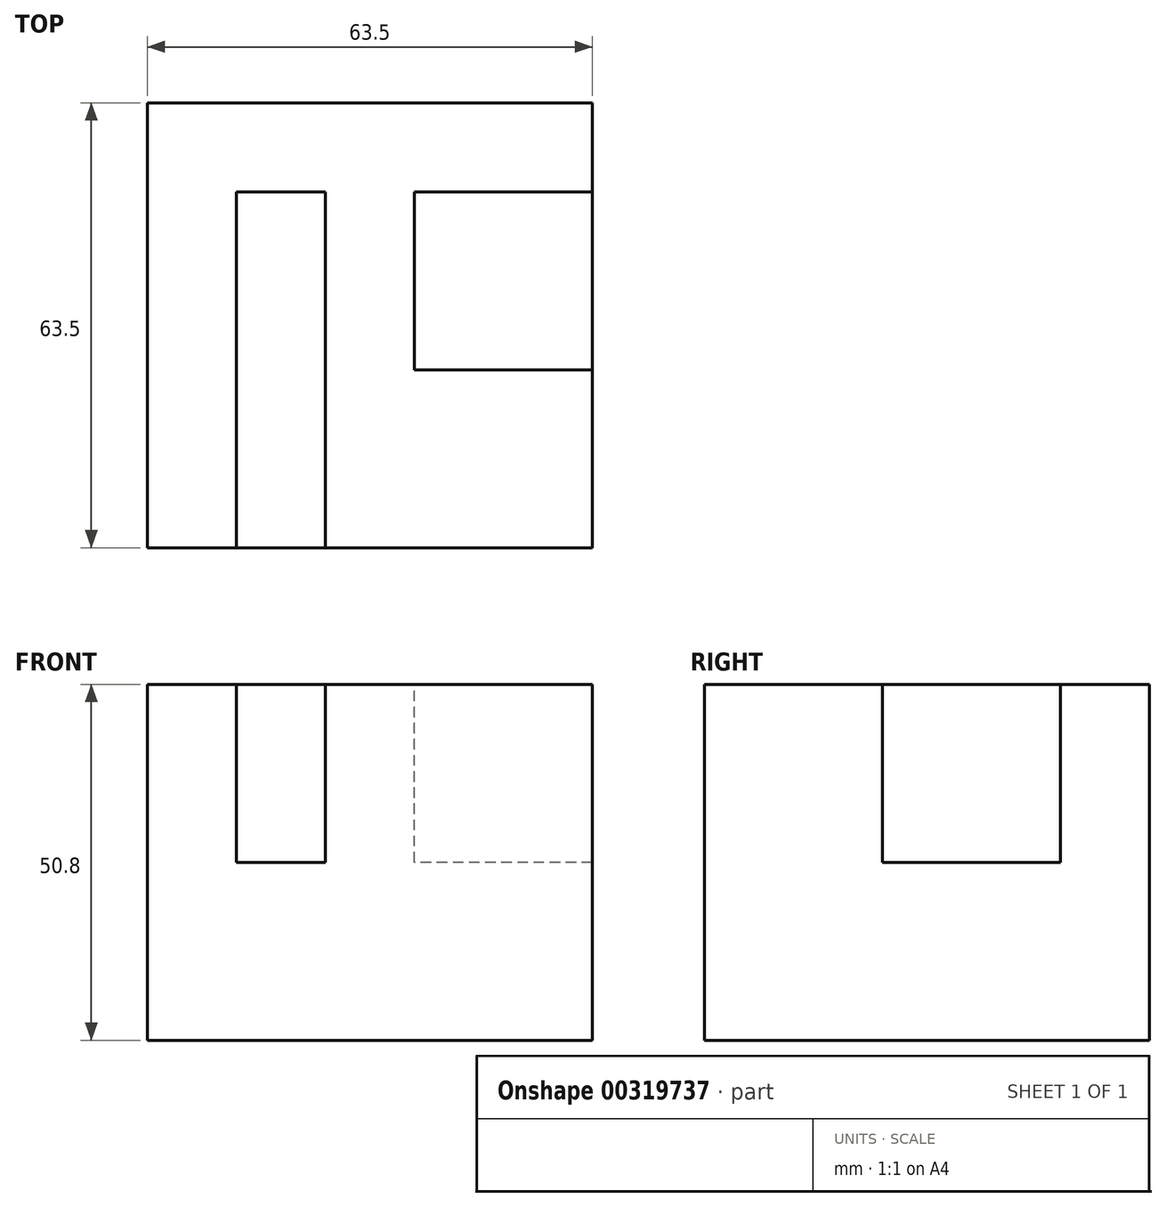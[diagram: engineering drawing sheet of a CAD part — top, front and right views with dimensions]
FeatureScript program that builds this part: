
annotation { "Feature Type Name" : "Feature", "Feature Type Description" : "" }
export const myFeature = defineFeature(function(context is Context, id is Id, definition is map)
    precondition{}
    {
        {
            var Q0;
            Q0=qCreatedBy(makeId("Top.planeOp"),FACE);
            var sketch = newSketch(context, id + "F0", { "sketchPlane" : qUnion([Q0])});
            skLineSegment(sketch, "E0", {"start": v(-27.52, -48.66) * mm, "end": v(35.98, -48.66) * mm});
            skLineSegment(sketch, "E1", {"start": v(35.98, -48.66) * mm, "end": v(35.98, 14.84) * mm});
            skLineSegment(sketch, "E2", {"start": v(35.98, 14.84) * mm, "end": v(-27.52, 14.84) * mm});
            skLineSegment(sketch, "E3", {"start": v(-27.52, 14.84) * mm, "end": v(-27.52, -48.66) * mm});
            skSolve(sketch);
        }
        {
            var Q0;
            Q0=makeQuery(id+"F0.imprint","IMPRINT",FACE,{"disambiguationData":[TD([[makeQuery(id+"F0.imprint","IMPRINT",EDGE,{"derivedFrom":sQuery(id+"F0.wireOp",EDGE,"E0")}),1.0]])]});
            extrude(context, id + "F1", {"entities" : qUnion([Q0]), "depth" : 50.8 * mm});
        }
        {
            var Q0;
            Q0=makeQuery(id+"F1.opExtrude","CAP_FACE",FACE,{"disambiguationData":[OSD([sQuery(id+"F0.wireOp",EDGE,"E0"),sQuery(id+"F0.wireOp",EDGE,"E1"),sQuery(id+"F0.wireOp",EDGE,"E2"),sQuery(id+"F0.wireOp",EDGE,"E3")])],"isStart":false});
            var sketch = newSketch(context, id + "F2", { "sketchPlane" : qUnion([Q0])});
            skLineSegment(sketch, "E4", {"start": v(-14.82, -48.66) * mm, "end": v(-14.82, 2.14) * mm});
            skLineSegment(sketch, "E5", {"start": v(-14.82, 2.14) * mm, "end": v(-2.12, 2.14) * mm});
            skLineSegment(sketch, "E6", {"start": v(-2.12, 2.14) * mm, "end": v(-2.12, -48.66) * mm});
            skLineSegment(sketch, "E7", {"start": v(35.98, 2.14) * mm, "end": v(10.58, 2.14) * mm});
            skLineSegment(sketch, "E8", {"start": v(10.58, 2.14) * mm, "end": v(10.58, -23.26) * mm});
            skLineSegment(sketch, "E9", {"start": v(10.58, -23.26) * mm, "end": v(35.98, -23.26) * mm});
            skLineSegment(sketch, "E10", {"start": v(35.98, -23.26) * mm, "end": v(35.98, 2.14) * mm});
            skSolve(sketch);
        }
        {
            var Q0;
            {var subQ0=sQuery(id+"F2.wireOp",EDGE,"E4");Q0=makeQuery(id+"F2.imprint","IMPRINT",FACE,{"disambiguationData":[TD([[makeQuery(id+"F2.imprint","IMPRINT",EDGE,{"derivedFrom":subQ0}),-1.0]])]});}
            var Q1;
            Q1=makeQuery(id+"F2.imprint","IMPRINT",FACE,{"disambiguationData":[TD([[makeQuery(id+"F2.imprint","IMPRINT",EDGE,{"derivedFrom":sQuery(id+"F2.wireOp",EDGE,"E7")}),1.0]])]});
            extrude(context, id + "F3", {"entities" : qUnion([Q0, Q1]), "operationType" : NewBodyOperationType.REMOVE, "oppositeDirection" : true, "depth" : 25.4 * mm});
        }
    });
